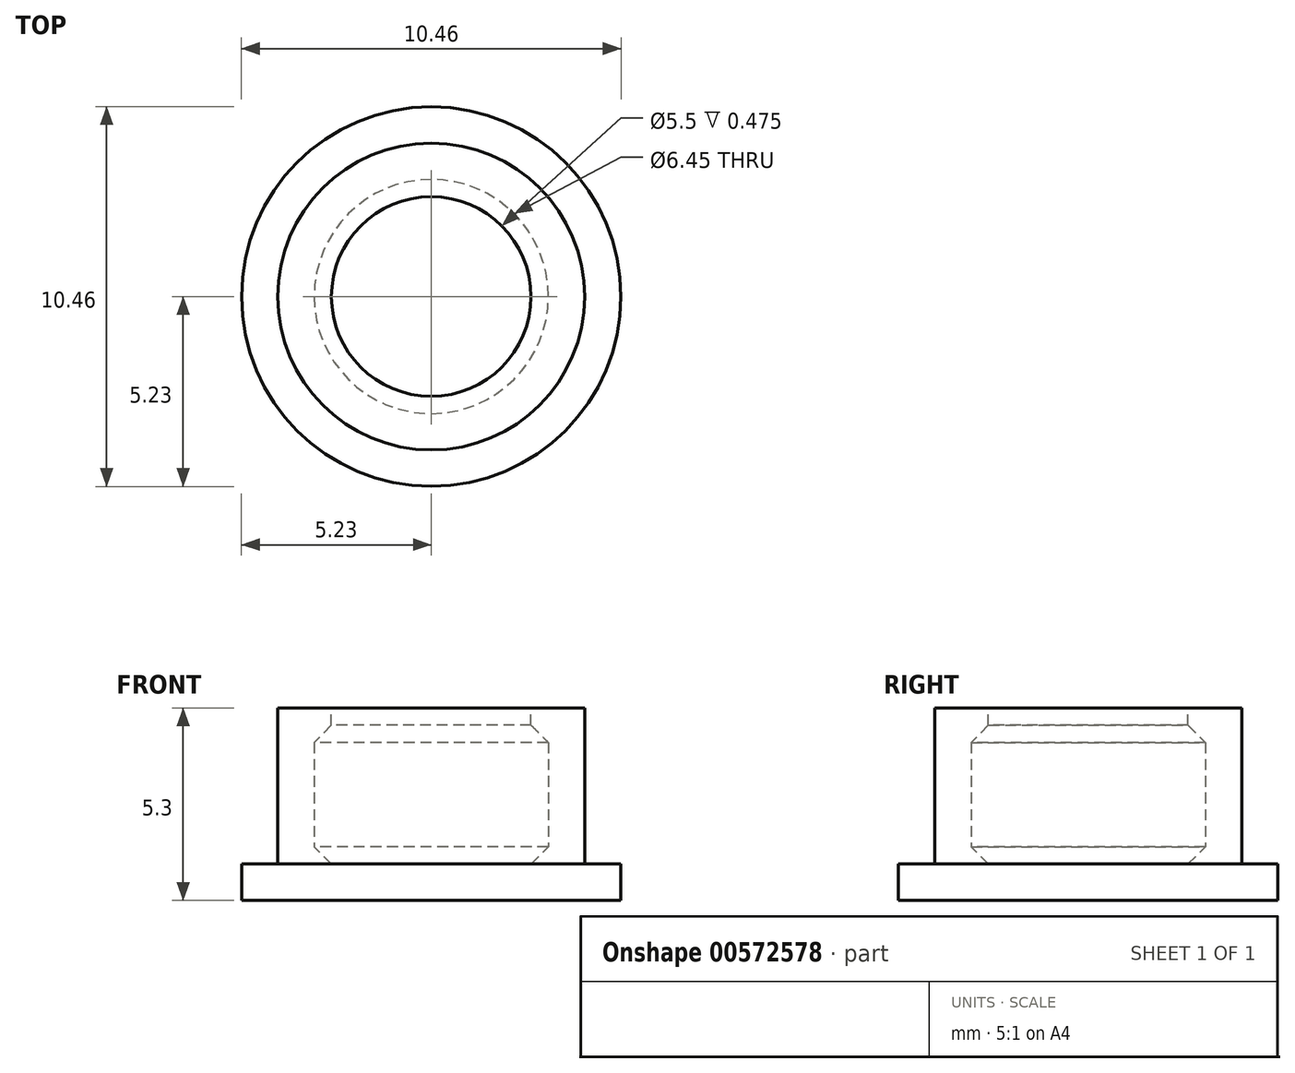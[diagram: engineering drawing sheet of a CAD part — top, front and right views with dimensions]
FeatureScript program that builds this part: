
annotation { "Feature Type Name" : "Feature", "Feature Type Description" : "" }
export const myFeature = defineFeature(function(context is Context, id is Id, definition is map)
    precondition{}
    {
        {
            assignVariable(context, id + "F0", {"name" : "zerk_height", "anyValue" : 4.3});
        }
        {
            assignVariable(context, id + "F1", {"name" : "zerk_width", "anyValue" : 6.45});
        }
        {
            assignVariable(context, id + "F2", {"name" : "zerk_ring", "anyValue" : 5.5});
        }
        {
            assignVariable(context, id + "F3", {"name" : "thickness", "anyValue" : 1});
        }
        {
            assignVariable(context, id + "F4", {"name" : "ring", "anyValue" : (getVariable(context, 'zerk_width') - getVariable(context, 'zerk_ring')) / 2});
        }
        {
            var Q0;
            Q0=qCreatedBy(makeId("Top.planeOp"),FACE);
            var sketch = newSketch(context, id + "F5", { "sketchPlane" : qUnion([Q0])});
            skCircle(sketch, "E0", {"center": v(0, 0) * mm, "radius": 4.22 * mm});
            skCircle(sketch, "E1", {"center": v(0, 0) * mm, "radius": 3.23 * mm});
            skSolve(sketch);
        }
        {
            var Q0;
            Q0=makeQuery(id+"F5.imprint","IMPRINT",FACE,{"disambiguationData":[TD([[makeQuery(id+"F5.imprint","IMPRINT",EDGE,{"derivedFrom":sQuery(id+"F5.wireOp",EDGE,"E0")}),1.0]])]});
            var sketch = newSketch(context, id + "F6", { "sketchPlane" : qUnion([Q0])});
            skCircle(sketch, "E2", {"center": v(0, 0) * mm, "radius": 5.22 * mm});
            skSolve(sketch);
        }
        {
            var Q0;
            Q0 = qSketchRegion(id + "F6", true);
            var Q1;
            Q1 = qSketchRegion(id + "F5", true);
            extrude(context, id + "F7", {"entities" : qUnion([Q0, Q1]), "depth" : (-getVariable(context, 'thickness')) * mm, "offsetDistance" : 25 * mm});
        }
        {
            var Q0;
            Q0=makeQuery(id+"F5.imprint","IMPRINT",FACE,{"disambiguationData":[TD([[makeQuery(id+"F5.imprint","IMPRINT",EDGE,{"derivedFrom":sQuery(id+"F5.wireOp",EDGE,"E0")}),1.0]])]});
            extrude(context, id + "F8", {"entities" : qUnion([Q0]), "operationType" : NewBodyOperationType.ADD, "depth" : (getVariable(context, 'zerk_height')) * mm, "offsetDistance" : 25 * mm});
        }
        {
            var Q0;
            Q0=makeQuery(id+"F8.opExtrude","CAP_FACE",FACE,{"disambiguationData":[OSD([sQuery(id+"F5.wireOp",EDGE,"E0"),sQuery(id+"F5.wireOp",EDGE,"E1")])],"isStart":false});
            var sketch = newSketch(context, id + "F9", { "sketchPlane" : qUnion([Q0])});
            skCircle(sketch, "E3", {"center": v(0, 0) * mm, "radius": 2.75 * mm});
            skSolve(sketch);
        }
        {
            var Q0;
            Q0=makeQuery(id+"F9.imprint","IMPRINT",FACE,{"disambiguationData":[TD([[makeQuery(id+"F9.imprint","IMPRINT",EDGE,{"derivedFrom":sQuery(id+"F9.wireOp",EDGE,"E3")}),-1.0]])]});
            extrude(context, id + "F10", {"entities" : qUnion([Q0]), "operationType" : NewBodyOperationType.ADD, "depth" : (-getVariable(context, 'ring') * 2) * mm, "offsetDistance" : 25 * mm});
        }
        {
            var Q0;
            Q0=makeQuery(id+"F10.opExtrude","CAP_EDGE",EDGE,{"disambiguationData":[OSD([sQuery(id+"F9.wireOp",EDGE,"E3")])],"isStart":false});
            chamfer(context, id + "F11", {"entities" : qUnion([Q0]), "width" : getVariable(context, 'ring') * mm, "tangentPropagation" : true});
        }
        {
            var Q0;
            Q0=makeQuery(id+"F8.boolean.opBoolean","SPLIT",FACE,{"disambiguationData":[TD([makeQuery(id+"F8.opExtrude","SWEPT_FACE",FACE,{"disambiguationData":[OSD([sQuery(id+"F5.wireOp",EDGE,"E1")])]})])],"derivedFrom":makeQuery(id+"F7.opExtrude","CAP_FACE",FACE,{"disambiguationData":[OSD([sQuery(id+"F6.wireOp",EDGE,"E2")])],"isStart":true})});
            chamfer(context, id + "F12", {"entities" : qUnion([Q0]), "width" : getVariable(context, 'ring') * mm, "tangentPropagation" : true});
        }
    });
